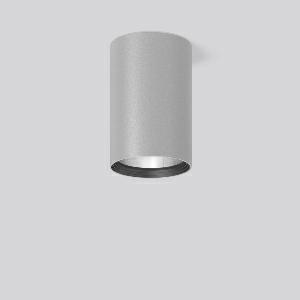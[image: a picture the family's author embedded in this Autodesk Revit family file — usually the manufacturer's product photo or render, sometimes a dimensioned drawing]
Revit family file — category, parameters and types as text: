
# Revit family: heledon_maxi_a_931224_004_2_2345
name_source: partatom
category: Lighting Fixtures
units: mm (PartAtom-declared; Revit-internal decimal feet)

## family parameters
Cut with Voids When Loaded = No
Host = Face
Light Source = No
Part Type = Normal
Room Calculation Point = No
Round Connector Dimension = Use Diameter
Shared = No

## types (1)
- HELEDON maxi A (1 x LED Modul 927, 4100 lm, 2700)
    Apparent Load = 35 VA
    Approval mark = CE
    CIE Flux Codes = 100 100 100 100 100
    Color Rendering = 92
    Color Temperature = 2700
    Default Elevation = 1800 mm
    Description = Series: HELEDON maxi
Cylindrical surface-mounted downlight. Housing: die-cast aluminium, powder-coated. Internal ceiling frame polycarbonate with bayonet mounting. Black plastic ring and recessed LED to prevent glare from the side. Optical assembly with reflector made of MIRO-Silver with 98% total light reflection for outstanding efficiency - can be changed without tools. Best colour rendering index Ra>90. Suitable for Ceiling mounting. Easy installation with a separate ceiling frame with bayonet mounting and plug connection. Driver integrated. Connected via plug-in connector. High quality converter without flickering and stroboscopic effect. The following accessories can be mounted without use of tools: interchangeable lenses, decorative glasses, honeycomb louvre, clear and frosted diffusers, white interchangeable plastic ring. 
Colour: silver
Diameter: 123 mm
Height: 183 mm
Lamp: LED
Socket: without socket
Colour temperature: 2700K
Colour rendering index (CRI): 92
System power: 35 W
Rated luminous flux: 4100 lm
Luminous efficiency: 117 lm/W
Control gear: Regulated power supply
Protection class: I
Type of protection: IP 20
    Height = 183 mm
    Lamp = 1 x LED Modul 927
    Lamp Light Flux = 4100 lm
    Lamp count = 1
    Length = 123 mm
    Lifetime = 50000 h
    Luminous efficacy = 117 lm/W
    Manufacturer = RZB
    ModVariant = No
    Model = 931224.004.2
    Mounting Place = Ceiling
    Mounting Type = Surface mounted
    Number of Poles = 1
    OnlyDefault = Yes
    Power Factor = 1
    Product Name = HELEDON maxi A
    Product group = Surface mounted downlights
    ProductGroupID = 302
    Protection Class = Protection class I
    Protection Degree = IP 20
    RLX_Detail_Level = 1
    RLX_Emergency_Light_Flux = 0 lm
    RLX_Emergency_Type = 0
    RLX_Emergency_Type_DB = No
    RlxData = <blob elided: 100757 chars, md5=9d45da85>
    Socket = socket
    Standby Power = 0 W
    System Light Flux = 4100 lm
    System Power = 35 W
    Type Comments = Product without accessories
    Type Image = 931192.004.jpg
    URL = http://relux.com
    VarID = ---
    Voltage = 230 V
    Voltage Range = 220-240 V
    Weight = 0.00 kg
    Width = 0 mm  [stored 0 ft]

note: [stored X ft] marks values corroborated as IEEE doubles in the binary element streams (Revit-internal decimal feet)

## geometry (parser evidence)
native form markers: Blend x4, Sweep x11
no freeform markers — native parametric forms only
